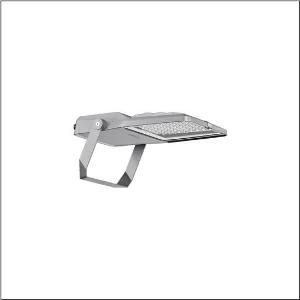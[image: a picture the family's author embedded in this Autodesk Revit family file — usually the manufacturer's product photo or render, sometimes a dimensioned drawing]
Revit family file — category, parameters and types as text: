
# Revit family: floodlight_fl_21_iq_mini___pl61_5xa7772b2c1a_d28a
name_source: partatom
category: Lighting Fixtures
units: mm (PartAtom-declared; Revit-internal decimal feet)

## family parameters
Cut with Voids When Loaded = No
Host = Face
Light Source = No
Part Type = Normal
Room Calculation Point = No
Round Connector Dimension = Use Diameter
Shared = No

## types (1)
- --- (1 x LED, 6120 lm, 45.5 W, 3000K)
    Apparent Load = 46 VA
    CIE Flux Codes = 33 65 98 100 100
    Color Rendering = 70
    Color Temperature = 3000K
    Default Elevation = 1800 mm
    Description = Floodlight FL 21 iQ mini, floodlight, primary light control with lens, of PMMA, primary optical cover: protective disc, of toughened safety glass, transparent, light distribution: PL61, light emission: direct distribution, installation type: surface-mounted, LED, High Power LED, rated luminous flux: 6.120lm, luminous efficacy: 135lm/W, light colour: 730, colour temperature: 3000K, control: Street-Remote, Auto-Match, Temp-Guard, Night-Set, Smart-Wire, Desk-Remote (wireless, voltage-free reading and setting of iQ features in the workshop via application-optimized NFC function/RFID function), optimised constant luminous flux control (CLO 2.0), with terminal, 6-pole, mains connection: 220..240V, AC, 50/60Hz, start of lifetime: 46W, end of service life: 48W, reduction: 22W, luminaire housing, of diecast aluminium, powder-coated, Siteco® metallic grey (DB 702S), corrosivity category C5 mid according to DIN EN ISO 12944, sealing non-destructively replaceable, mounting bracket, of steel, galvanised, powder-coated, Siteco® metallic grey (DB 702S), protection rating (complete): IP66, insulation class (complete): insulation class II (safety insulation), certification: CE, ENEC, VDE, protection symbol: D, impact resistance: IK08, permissible operating ambient temperature: -40..+40°C, permissible operating ambient temperature for outdoor applications: -40..+50°C, standard: DIN EN 12944, LABS conformity tested according to VDMA 24364:2018-05, packaging unit: 1 piece

Light Distribution: PL61
    Height = 70 mm
    Lamp = 1 x LED
    Lamp Light Flux = 6120 lm
    Lamp Power = 45.5 W
    Lamp count = 1
    Length = 485 mm
    Luminous efficacy = 135 lm/W
    Manufacturer = Siteco
    ModVariant = No
    Model = 5XA7772B2C1A
    Number of Poles = 1
    OnlyDefault = Yes
    Power Factor = 1
    Product Name = Floodlight FL 21 iQ mini | PL61
    Product group = floodlight | pylon annexe
    ProductGroupID = 6200
    Protection Class = Protection class II
    Protection Degree = IP 66
    RLX_Detail_Level = 1
    RLX_Emergency_Light_Flux = 0 lm
    RLX_Emergency_Type = 0
    RLX_Emergency_Type_DB = No
    RlxData = <blob elided: 96101 chars, md5=53c3121e>
    Socket = socket
    Standby Power = 0 W
    System Light Flux = 6120 lm
    System Power = 46 W
    Type Comments = factory setting: luminous flux: 100 % | dim-lin: 254 | 463 mA
    Type Image = l_1006845.jpg
    URL = http://relux.com
    VarID = @adj_106731
    Voltage = 0 V
    Weight = 0.00 kg
    Width = 337 mm

## geometry (parser evidence)
native form markers: Blend x4, Sweep x11
no freeform markers — native parametric forms only
